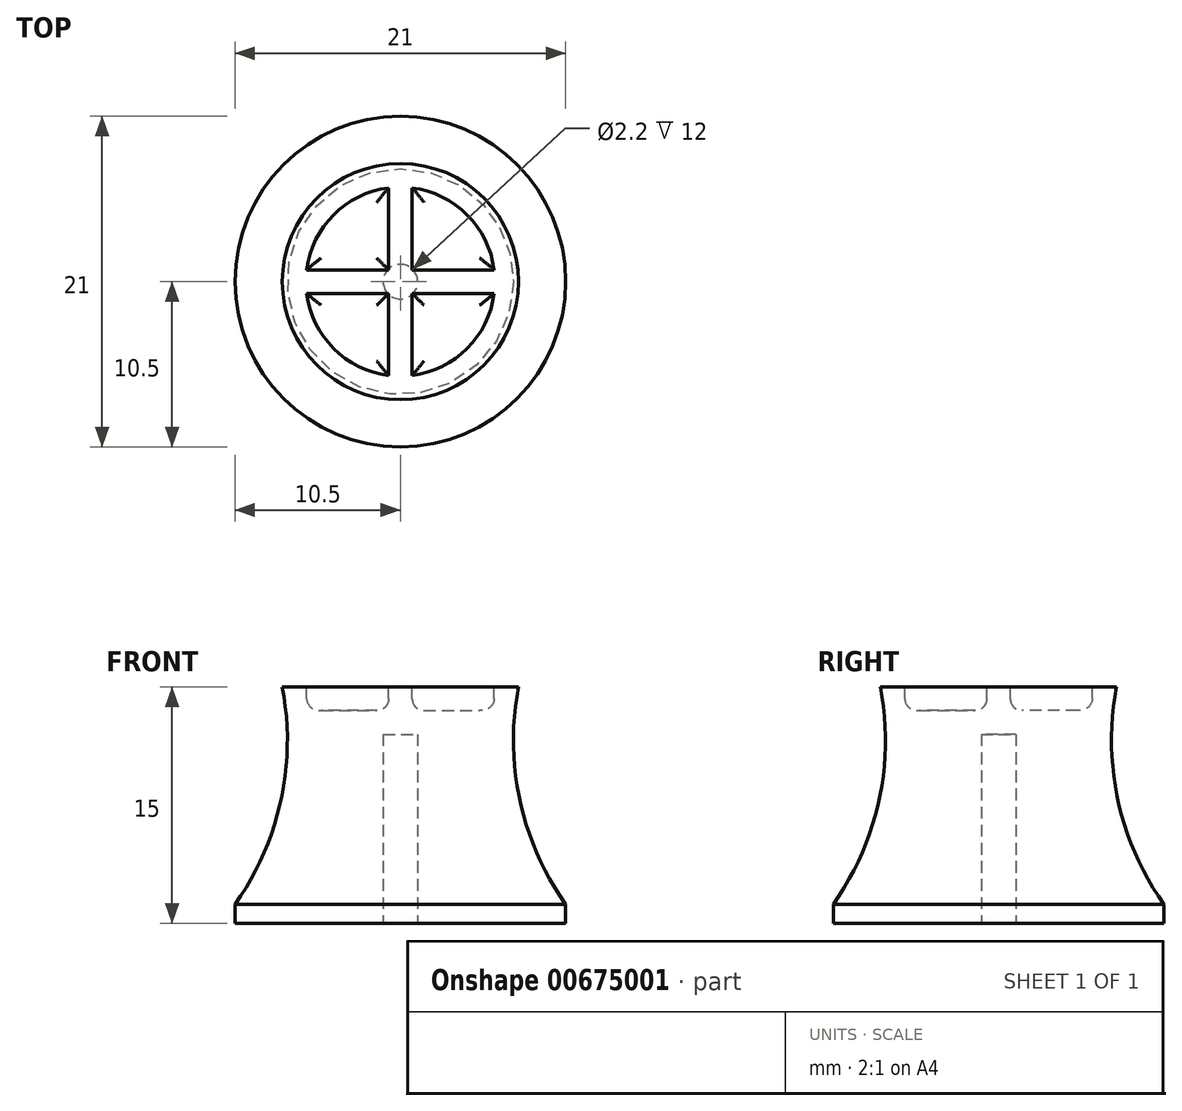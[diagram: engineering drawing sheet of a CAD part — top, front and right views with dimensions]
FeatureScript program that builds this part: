
annotation { "Feature Type Name" : "Feature", "Feature Type Description" : "" }
export const myFeature = defineFeature(function(context is Context, id is Id, definition is map)
    precondition{}
    {
        {
            assignVariable(context, id + "F0", {"name" : "Faktor", "anyValue" : 1.5});
        }
        {
            var Q0;
            Q0=qCreatedBy(makeId("Right.planeOp"),FACE);
            var sketch = newSketch(context, id + "F1", { "sketchPlane" : qUnion([Q0])});
            skLineSegment(sketch, "E0", {"start": v(0, 0) * mm, "end": v(-10.5, 0) * mm});
            skLineSegment(sketch, "E1", {"start": v(0, 0) * mm, "end": v(0, 15) * mm});
            skLineSegment(sketch, "E2", {"start": v(0, 15) * mm, "end": v(-7.5, 15) * mm});
            skLineSegment(sketch, "E3", {"start": v(0, 24.51) * mm, "end": v(0, -9.99) * mm, "construction": true});
            skLineSegment(sketch, "E4", {"start": v(-10.5, 0) * mm, "end": v(-10.5, 1.2) * mm});
            skArc(sketch, "E5", {"start": v(-10.5, 1.2) * mm, "mid": v(-7.6, 7.8) * mm, "end": v(-7.5, 15) * mm});
            skSolve(sketch);
        }
        {
            var Q0;
            Q0=qSketchRegion(id+"F1",true);
            var Q1;
            Q1=sQuery(id+"F1.wireOp",EDGE,"E3");
            revolve(context, id + "F2", {"entities" : qUnion([Q0]), "axis" : qUnion([Q1]), "revolveType" : RevolveType.FULL});
        }
        {
            var Q0;
            Q0=makeQuery(id+"F2.opRevolve","SWEPT_FACE",FACE,{"disambiguationData":[OSD([sQuery(id+"F1.wireOp",EDGE,"E0")])]});
            var sketch = newSketch(context, id + "F3", { "sketchPlane" : qUnion([Q0])});
            skCircle(sketch, "E6", {"center": v(0, 0) * mm, "radius": 1.1 * mm});
            skSolve(sketch);
        }
        {
            var Q0;
            Q0=qSketchRegion(id+"F3",true);
            extrude(context, id + "F4", {"entities" : qUnion([Q0]), "operationType" : NewBodyOperationType.REMOVE, "oppositeDirection" : true, "depth" : getVariable(context, 'Faktor') * 8 * mm, "offsetDistance" : 25 * mm});
        }
        {
            var Q0;
            Q0=makeQuery(id+"F2.opRevolve","SWEPT_FACE",FACE,{"disambiguationData":[OSD([sQuery(id+"F1.wireOp",EDGE,"E2")])]});
            var sketch = newSketch(context, id + "F5", { "sketchPlane" : qUnion([Q0])});
            skArc(sketch, "E7", {"start": v(-0.75, 5.95) * mm, "mid": v(-4.24, 4.24) * mm, "end": v(-5.95, 0.75) * mm});
            skLineSegment(sketch, "E8", {"start": v(0.75, 5.95) * mm, "end": v(0.75, 0.75) * mm});
            skLineSegment(sketch, "E9", {"start": v(-0.75, 5.95) * mm, "end": v(-0.75, 0.75) * mm});
            skLineSegment(sketch, "E10", {"start": v(-5.95, 0.75) * mm, "end": v(-0.75, 0.75) * mm});
            skLineSegment(sketch, "E11", {"start": v(-5.95, -0.75) * mm, "end": v(-0.75, -0.75) * mm});
            skArc(sketch, "E12.trimOffspring", {"start": v(-5.95, -0.75) * mm, "mid": v(-4.24, -4.24) * mm, "end": v(-0.75, -5.95) * mm});
            skArc(sketch, "E13.trimOffspring", {"start": v(0.75, -5.95) * mm, "mid": v(4.24, -4.24) * mm, "end": v(5.95, -0.75) * mm});
            skArc(sketch, "E14.trimOffspring", {"start": v(5.95, 0.75) * mm, "mid": v(4.24, 4.24) * mm, "end": v(0.75, 5.95) * mm});
            skLineSegment(sketch, "E15.trimOffspring", {"start": v(0.75, -0.75) * mm, "end": v(0.75, -5.95) * mm});
            skLineSegment(sketch, "E16.trimOffspring", {"start": v(0.75, 0.75) * mm, "end": v(5.95, 0.75) * mm});
            skLineSegment(sketch, "E17.trimOffspring", {"start": v(-0.75, -0.75) * mm, "end": v(-0.75, -5.95) * mm});
            skLineSegment(sketch, "E18.trimOffspring", {"start": v(0.75, -0.75) * mm, "end": v(5.95, -0.75) * mm});
            skSolve(sketch);
        }
        {
            var Q0;
            Q0=qSketchRegion(id+"F5",true);
            extrude(context, id + "F6", {"entities" : qUnion([Q0]), "operationType" : NewBodyOperationType.REMOVE, "oppositeDirection" : true, "depth" : getVariable(context, 'Faktor') * 1 * mm, "offsetDistance" : 25 * mm});
        }
        {
            var Q0;
            Q0=makeQuery(id+"F6.boolean.opBoolean","COPY",FACE,{"derivedFrom":makeQuery(id+"F6.opExtrude","CAP_FACE",FACE,{"disambiguationData":[OSD([sQuery(id+"F5.wireOp",EDGE,"E7"),sQuery(id+"F5.wireOp",EDGE,"E9"),sQuery(id+"F5.wireOp",EDGE,"E10")])],"isStart":false})});
            var Q1;
            Q1=makeQuery(id+"F6.boolean.opBoolean","COPY",FACE,{"derivedFrom":makeQuery(id+"F6.opExtrude","CAP_FACE",FACE,{"disambiguationData":[OSD([sQuery(id+"F5.wireOp",EDGE,"E8"),sQuery(id+"F5.wireOp",EDGE,"E14.trimOffspring"),sQuery(id+"F5.wireOp",EDGE,"E16.trimOffspring")])],"isStart":false})});
            var Q2;
            Q2=makeQuery(id+"F6.boolean.opBoolean","COPY",FACE,{"derivedFrom":makeQuery(id+"F6.opExtrude","CAP_FACE",FACE,{"disambiguationData":[OSD([sQuery(id+"F5.wireOp",EDGE,"E13.trimOffspring"),sQuery(id+"F5.wireOp",EDGE,"E15.trimOffspring"),sQuery(id+"F5.wireOp",EDGE,"E18.trimOffspring")])],"isStart":false})});
            var Q3;
            Q3=makeQuery(id+"F6.boolean.opBoolean","COPY",FACE,{"derivedFrom":makeQuery(id+"F6.opExtrude","CAP_FACE",FACE,{"disambiguationData":[OSD([sQuery(id+"F5.wireOp",EDGE,"E11"),sQuery(id+"F5.wireOp",EDGE,"E12.trimOffspring"),sQuery(id+"F5.wireOp",EDGE,"E17.trimOffspring")])],"isStart":false})});
            fillet(context, id + "F7", {"entities" : qUnion([Q0, Q1, Q2, Q3]), "radius" : getVariable(context, 'Faktor') * 0.5 * mm, "tangentPropagation" : true, "allowEdgeOverflow" : false});
        }
    });
